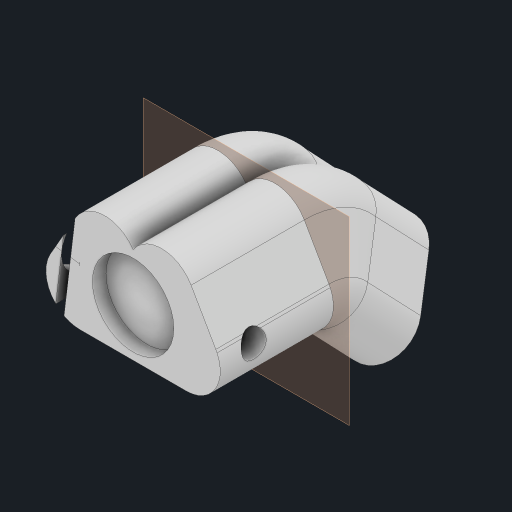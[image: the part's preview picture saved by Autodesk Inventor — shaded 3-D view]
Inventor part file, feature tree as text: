
AUTODESK INVENTOR PART (.ipt)
format: ipt  version: 2023 (Build 270158000, 158)  size: 529,408 bytes
history: native  units: mm
features: extrude x14, sketch x10, plane x4, chamfer x2, mirror x1, revolve x1
ambient origin geometry x8: Origin, YZ Plane, XZ Plane, XY Plane, X Axis, Y Axis, Z Axis, Center Point
bodies: Solid1 (feature_tree)
feature tree (32):
  sketch  "Sketch1"  dims[d0=100.0mm d1=25.0mm d2=7.5mm d3=7.5mm d4=60.0deg d5=15.0mm d6=11.0mm d7=11.0mm d8=15.0mm d14=4.0mm d15=0.0mm]
  extrude  "Extrusion1"  Depth=7.5mm TaperAngle=0.0deg
  plane  "Work Plane13"
  sketch  "Sketch7"  dims[d72=7.5mm d73=90.0deg]
  extrude  "Extrusion6"  TaperAngle=90.0deg  [1 undecoded]
  extrude  "Extrusion7"  Depth=7.5mm
  mirror  "Mirror4"
  plane  "Work Plane9"
  extrude  "Extrusion8"  Depth=15.0mm
  revolve  "Revolution2"  [1 undecoded]
  extrude  "Extrusion9"  Depth=6.5mm
  extrude  "Extrusion10"  Depth=15.0mm TaperAngle=0.0deg
  extrude  "Extrusion11"  Depth=10.0mm TaperAngle=0.0deg
  chamfer  "Chamfer3"  Distance=4.0mm
  chamfer  "Chamfer4"  Distance=10.0mm
  plane  "Work Plane16"
  extrude  "Extrusion14"  Depth=10.0mm TaperAngle=45.0deg
  extrude  "Extrusion15"  Depth=10.0mm TaperAngle=45.0deg
  sketch  "Sketch32"  dims[d93=10.0mm d94=0.0mm d115=20.0mm d116=0.0mm]
  extrude  "Extrusion21"  Depth=10.0mm
  extrude  "Extrusion22"  Depth=10.0mm
  extrude  "Extrusion23"  Depth=10.0mm
  extrude  "Extrusion25"  Depth=25.0mm TaperAngle=0.0deg
  plane  "Work Plane18"
  extrude  "Extrusion26"  Depth=10.0mm
  sketch  "Sketch14"  dims[d74=7.5mm d75=5.5mm]
  sketch  "Sketch15"  dims[d76=5.5mm d77=15.0mm]
  sketch  "Sketch19"  dims[d78=11.0mm d79=11.0mm]
  sketch  "Sketch23"  dims[d80=2.0mm d81=6.5mm]
  sketch  "Sketch24"  dims[d82=6.5mm d83=15.0mm d84=0.0mm]
  sketch  "Sketch34"  dims[d131=8.648979mm d132=4.0mm d133=0.0mm d134=10.0mm d135=0.0mm]
  sketch  "Sketch35"  dims[d136=10.0mm d137=0.0mm d138=2.0mm d139=4.0mm d140=45.0deg d141=2.0mm d142=4.0mm d143=45.0deg d153=15.0mm d154=15.0mm d155=15.0mm d156=25.0mm d157=0.0mm d158=20.0mm d160=20.0mm d161=10.0mm d168=30.0mm d169=0.0mm d173=2.0mm d221=10.93871mm d243=1.21824mm d247=15.0mm d248=20.0mm d249=15.0mm d250=15.0mm d251=15.0mm d252=5.5mm d253=20.0mm d254=0.0mm d255=2.0mm d256=0.0mm d257=50.0mm d258=0.0mm d266=90.0deg d267=18.0mm d268=3.0mm d269=0.0mm d270=3.4mm d271=18.0mm d272=6.0mm d273=0.0mm d274=3.0mm d275=0.0mm d182=0.5mm d183=0.872665mm d184=0.5mm d185=0.872665mm d224=0.5mm d225=0.872665mm d226=0.5mm d227=0.872665mm]
note: 2 required parameter values undecoded (feature->parameter linkage not recoverable at this tier; creation-order binding heuristic only, values carry confidence <= 0.55)